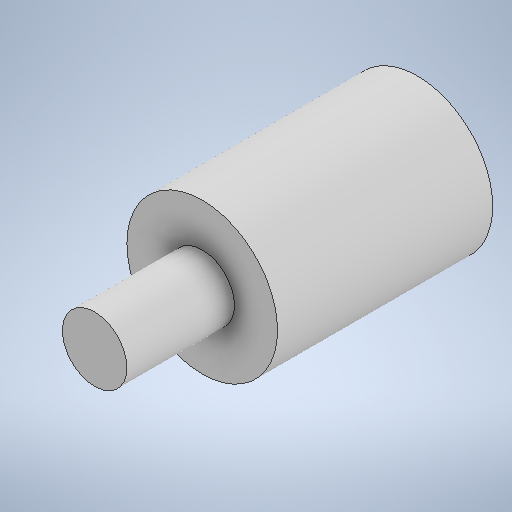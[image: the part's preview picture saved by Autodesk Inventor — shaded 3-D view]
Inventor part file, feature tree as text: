
AUTODESK INVENTOR PART (.ipt)
format: ipt  version: 2025.3 (Build 293356000, 356)  size: 223,232 bytes
history: native  units: mm
features: extrude x3, sketch x3, other x1
ambient origin geometry x8: Origin, YZ Plane, XZ Plane, XY Plane, X Axis, Y Axis, Z Axis, Center Point
bodies: Body1 (feature_tree)
feature tree (7):
  other  "Sólido1"
  extrude  "Extrusión1"  Depth=20.0mm TaperAngle=0.0deg
  extrude  "Extrusión2"  Depth=2.5mm TaperAngle=0.0deg
  extrude  "Extrusión3"  Depth=10.0mm TaperAngle=0.0deg
  sketch  "Boceto1"  dims[d0=14.0mm d1=20.0mm d2=0.0mm]
  sketch  "Boceto2"  dims[d3=2.0mm d4=2.5mm d5=0.0mm]
  sketch  "Boceto3"  dims[d6=6.0mm d7=10.0mm d8=0.0mm]
